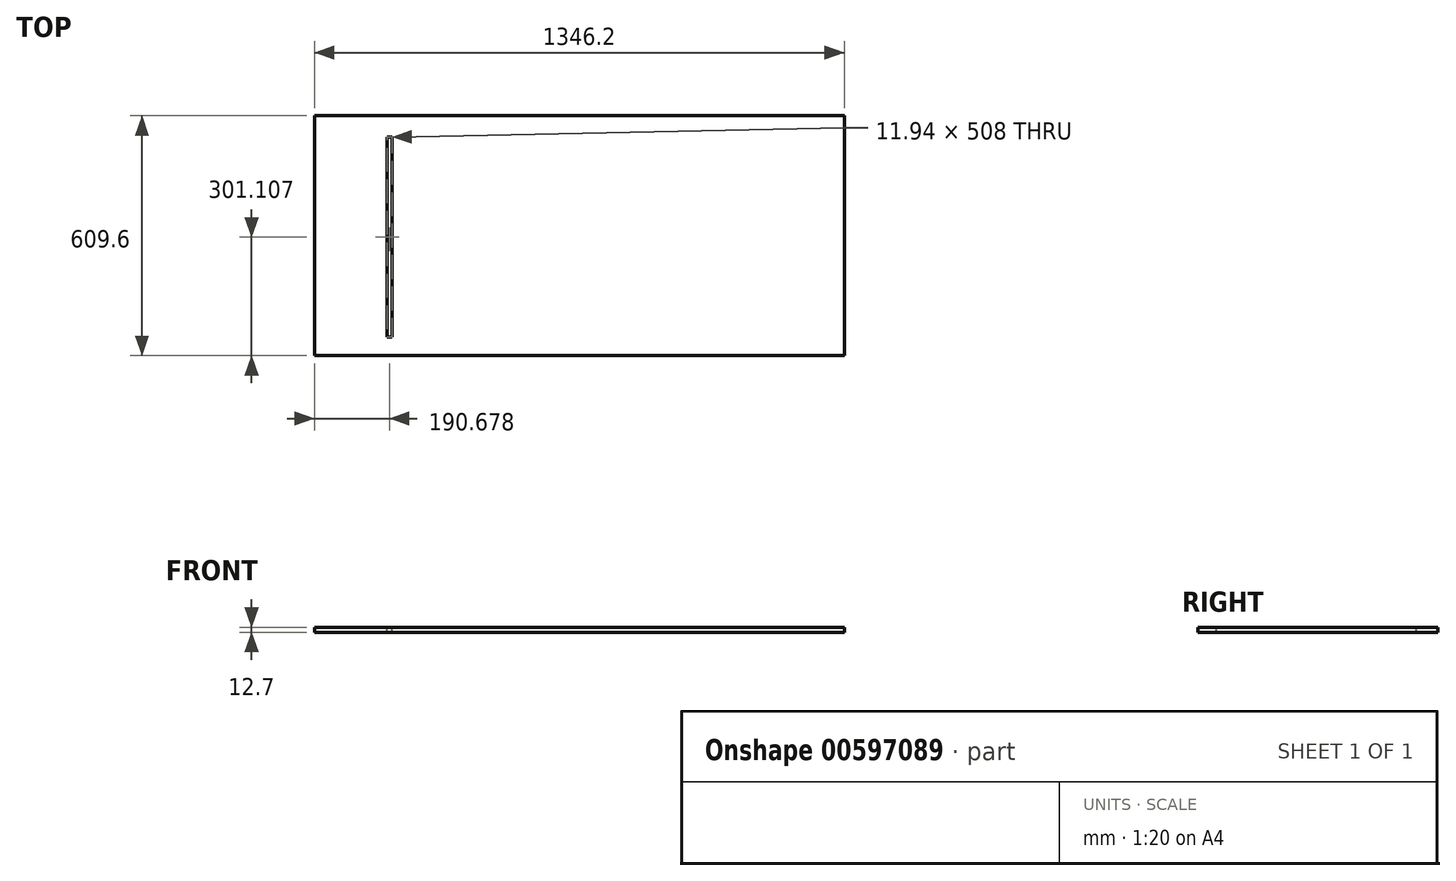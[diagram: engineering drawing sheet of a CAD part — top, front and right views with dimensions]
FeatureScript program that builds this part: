
annotation { "Feature Type Name" : "Feature", "Feature Type Description" : "" }
export const myFeature = defineFeature(function(context is Context, id is Id, definition is map)
    precondition{}
    {
        {
            var Q0;
            Q0=qCreatedBy(makeId("Top.planeOp"),FACE);
            var sketch = newSketch(context, id + "F0", { "sketchPlane" : qUnion([Q0])});
            skLineSegment(sketch, "E0.bottom", {"start": v(-673.36, 201.33) * mm, "end": v(672.84, 201.33) * mm});
            skLineSegment(sketch, "E0.top", {"start": v(-673.36, -408.27) * mm, "end": v(672.84, -408.27) * mm});
            skLineSegment(sketch, "E0.left", {"start": v(-673.36, 201.33) * mm, "end": v(-673.36, -408.27) * mm});
            skLineSegment(sketch, "E0.right", {"start": v(672.84, 201.33) * mm, "end": v(672.84, -408.27) * mm});
            skSolve(sketch);
        }
        {
            var Q0;
            Q0=makeQuery(id+"F0.imprint","IMPRINT",FACE,{"disambiguationData":[TD([[makeQuery(id+"F0.imprint","IMPRINT",EDGE,{"derivedFrom":sQuery(id+"F0.wireOp",EDGE,"E0.bottom")}),-1.0]])]});
            extrude(context, id + "F1", {"entities" : qUnion([Q0]), "depth" : 12.7 * mm, "offsetDistance" : 25.4 * mm});
        }
        {
            var Q0;
            Q0=makeQuery(id+"F1.opExtrude","CAP_FACE",FACE,{"disambiguationData":[OSD([sQuery(id+"F0.wireOp",EDGE,"E0.bottom"),sQuery(id+"F0.wireOp",EDGE,"E0.top"),sQuery(id+"F0.wireOp",EDGE,"E0.left"),sQuery(id+"F0.wireOp",EDGE,"E0.right")])],"isStart":false});
            var sketch = newSketch(context, id + "F2", { "sketchPlane" : qUnion([Q0])});
            skLineSegment(sketch, "E1.bottom", {"start": v(-488.65, 146.84) * mm, "end": v(-476.71, 146.84) * mm});
            skLineSegment(sketch, "E1.top", {"start": v(-488.65, -361.16) * mm, "end": v(-476.71, -361.16) * mm});
            skLineSegment(sketch, "E1.left", {"start": v(-488.65, 146.84) * mm, "end": v(-488.65, -361.16) * mm});
            skLineSegment(sketch, "E1.right", {"start": v(-476.71, 146.84) * mm, "end": v(-476.71, -361.16) * mm});
            skSolve(sketch);
        }
        {
            var Q0;
            Q0 = qSketchRegion(id + "F2", true);
            extrude(context, id + "F3", {"entities" : qUnion([Q0]), "operationType" : NewBodyOperationType.REMOVE, "oppositeDirection" : true, "depth" : 25.4 * mm, "offsetDistance" : 25.4 * mm});
        }
    });
